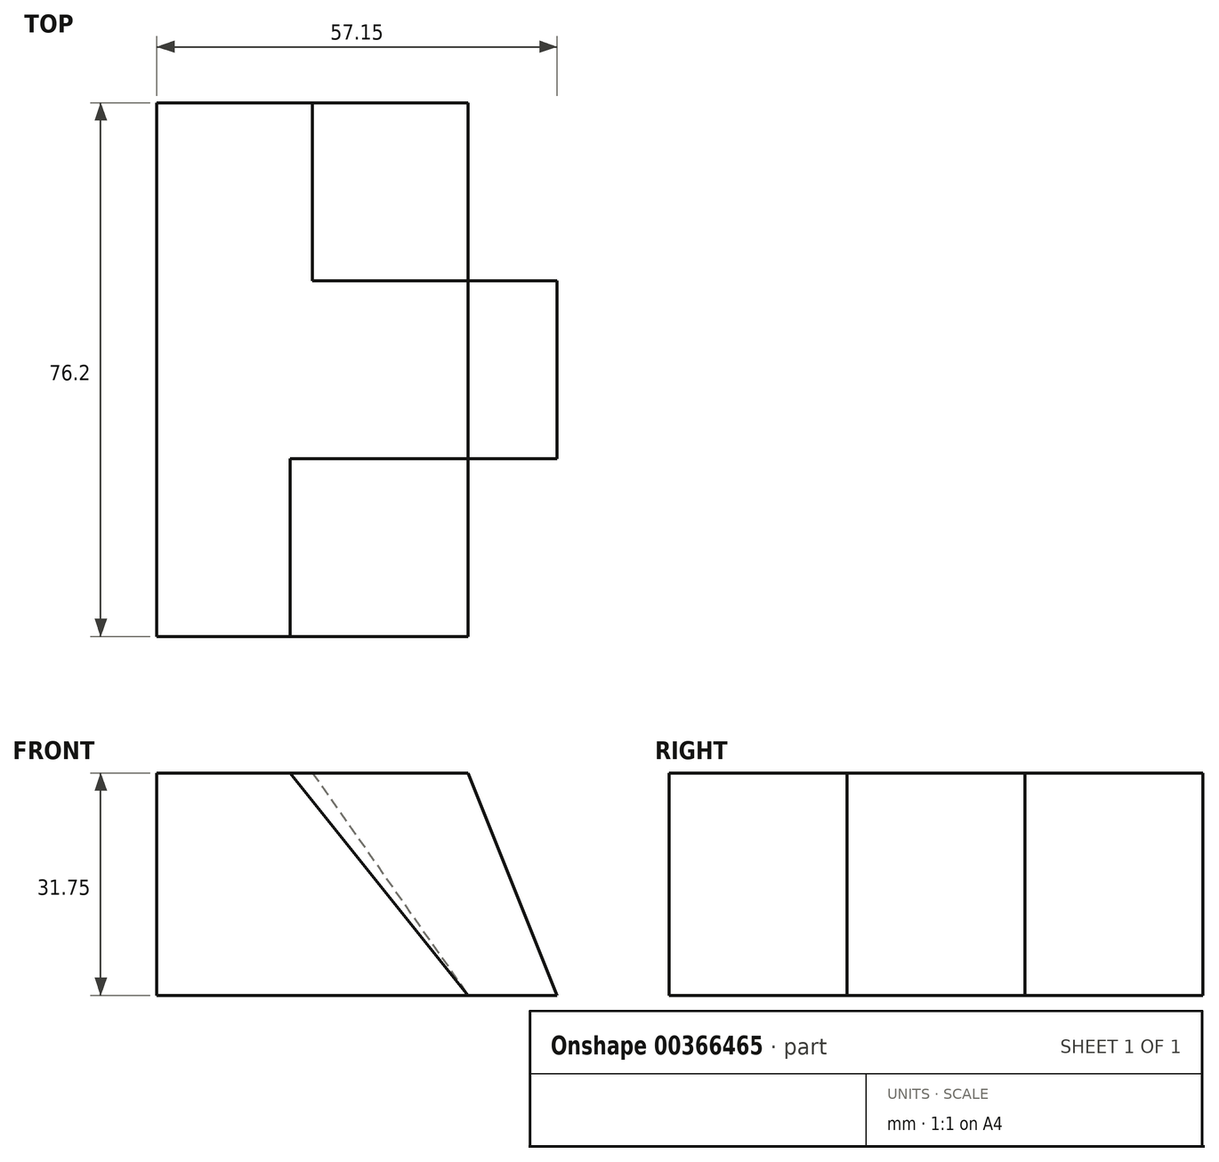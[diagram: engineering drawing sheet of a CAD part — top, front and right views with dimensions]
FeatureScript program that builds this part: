
annotation { "Feature Type Name" : "Feature", "Feature Type Description" : "" }
export const myFeature = defineFeature(function(context is Context, id is Id, definition is map)
    precondition{}
    {
        {
            var Q0;
            Q0=qCreatedBy(makeId("Front.planeOp"),FACE);
            var sketch = newSketch(context, id + "F0", { "sketchPlane" : qUnion([Q0])});
            skLineSegment(sketch, "E0", {"start": v(0, 0) * mm, "end": v(0, 31.75) * mm});
            skLineSegment(sketch, "E1", {"start": v(0, 31.75) * mm, "end": v(44.45, 31.75) * mm});
            skLineSegment(sketch, "E2", {"start": v(44.45, 31.75) * mm, "end": v(57.15, 0) * mm});
            skLineSegment(sketch, "E3", {"start": v(57.15, 0) * mm, "end": v(0, 0) * mm});
            skSolve(sketch);
        }
        {
            var Q0;
            Q0=makeQuery(id+"F0.imprint","IMPRINT",FACE,{"disambiguationData":[TD([[makeQuery(id+"F0.imprint","IMPRINT",EDGE,{"derivedFrom":sQuery(id+"F0.wireOp",EDGE,"E0")}),-1.0]])]});
            extrude(context, id + "F1", {"entities" : qUnion([Q0]), "depth" : 25.4 * mm});
        }
        {
            var Q0;
            Q0=makeQuery(id+"F1.opExtrude","CAP_FACE",FACE,{"disambiguationData":[OSD([sQuery(id+"F0.wireOp",EDGE,"E0"),sQuery(id+"F0.wireOp",EDGE,"E1"),sQuery(id+"F0.wireOp",EDGE,"E2"),sQuery(id+"F0.wireOp",EDGE,"E3")])],"isStart":false});
            var sketch = newSketch(context, id + "F2", { "sketchPlane" : qUnion([Q0])});
            skLineSegment(sketch, "E4", {"start": v(0, 0) * mm, "end": v(0, 31.75) * mm});
            skLineSegment(sketch, "E5", {"start": v(0, 31.75) * mm, "end": v(19.05, 31.75) * mm});
            skLineSegment(sketch, "E6", {"start": v(19.05, 31.75) * mm, "end": v(44.45, 0) * mm});
            skLineSegment(sketch, "E7", {"start": v(44.45, 0) * mm, "end": v(0, 0) * mm});
            skSolve(sketch);
        }
        {
            var Q0;
            Q0 = qSketchRegion(id + "F2", true);
            extrude(context, id + "F3", {"entities" : qUnion([Q0]), "operationType" : NewBodyOperationType.ADD, "depth" : 25.4 * mm});
        }
        {
            var Q0;
            Q0=makeQuery(id+"F1.opExtrude","CAP_FACE",FACE,{"disambiguationData":[OSD([sQuery(id+"F0.wireOp",EDGE,"E0"),sQuery(id+"F0.wireOp",EDGE,"E1"),sQuery(id+"F0.wireOp",EDGE,"E2"),sQuery(id+"F0.wireOp",EDGE,"E3")])],"isStart":true});
            var sketch = newSketch(context, id + "F4", { "sketchPlane" : qUnion([Q0])});
            skLineSegment(sketch, "E8", {"start": v(0, 0) * mm, "end": v(0, 31.75) * mm});
            skLineSegment(sketch, "E9", {"start": v(0, 31.75) * mm, "end": v(-22.23, 31.75) * mm});
            skLineSegment(sketch, "E10", {"start": v(-22.23, 31.75) * mm, "end": v(-44.45, 0) * mm});
            skLineSegment(sketch, "E11", {"start": v(-44.45, 0) * mm, "end": v(0, 0) * mm});
            skSolve(sketch);
        }
        {
            var Q0;
            Q0 = qSketchRegion(id + "F4", true);
            extrude(context, id + "F5", {"entities" : qUnion([Q0]), "operationType" : NewBodyOperationType.ADD, "depth" : 25.4 * mm});
        }
    });
